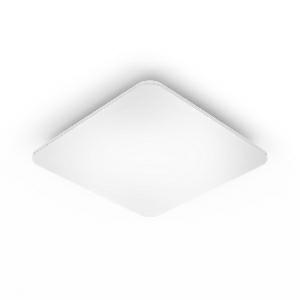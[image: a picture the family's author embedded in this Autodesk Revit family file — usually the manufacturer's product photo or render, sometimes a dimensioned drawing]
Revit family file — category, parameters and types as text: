
# Revit family: rs_pro_led_q1_007133
name_source: partatom
category: Leuchten
revit_build: Autodesk Revit 2016 (Build: 20190508_0715(x64)
units: mm (PartAtom-declared; Revit-internal decimal feet)

## family parameters
Basisbauteil = Fläche
Beim Laden mit Abzugskörper schneiden = Nein
Bemaßung runder Anschluss = Durchmesser verwenden
Gemeinsam genutzt = Nein
Lichtquelle = Nein
Raumberechnungspunkt = Nein
Teiletyp = Normal

## types (1)
- RS PRO LED Q1 (1 x , 2350 lm, 3000 K)
    Beschreibung = Dimensions (L x W x H): 56 x 331 x 331 mm; Mains power supply: 220 – 240 V / 50 – 60 Hz; Sensor Technology: High frequency; Transmitter power: < 1 mW; HF-system: 5,8 GHz; Output: 26 W; Interconnection: Yes; Type of interconnection: Master/master, Master/slave; Luminous flux: 2350 lm; Colour temperature: 3000 K; Colour variation LED: SDCM3; Colour Rendering Index CRI: 80-89; With lamp: Yes, STEINEL LED system; Lamp: LED cannot be replaced; LED life expectancy (max. °C): 50000 h; Drop in luminous flux in accordance with LM80: L70B10; Base: without; LED cooling system: Passive Thermo Control; With motion detector: Yes; Detection: also through glass, wood and stud walls; Detection angle: 360 °; Angle of aperture: 160 °; Capability of masking out individual segments: Yes; Electronic scalability: Yes; Mechanical scalability: No; Reach, radial: Ø 8 m (50 m²); Reach, tangential: Ø 8 m (50 m²); Main light adjustable: 50 - 100 %; Continuous light: selectable; Photo-cell controller: Yes; Twilight setting: 2 – 2000 lx; Time setting: 5 sec – 15 min; Basic light level function: Yes; Basic light level function time: 10/30 min, all night; Functions: Group parameterisation, Manual ON / ON-OFF, Master/slave override, Neighbouring-group function; Soft light start: Yes; Impact resistance: IK03; IP-rating: IP20; Protection class: II; Ambient temperature: -10 – 50 °C; Housing material: Aluminium; Cover material: Plastic, opal; Manufacturer's Warranty: 5 years; Settings via: DIP switches, Potentiometers, Remote control, Smart Remote; With remote control: No; Version: warm white white; PU1, EAN: 4007841007133
    CIE Flux Codes = 46 77 95 100 100
    Color Rendering = 80-89
    Color Temperature = 3000 K
    Frequency = 50 Hz, 60 Hz
    Height = 331 mm
    Hersteller = Steinel
    Lamp Light Flux = 2350 lm
    Lamp count = 1
    Lampe = 1 x
    Length = 56 mm  [stored 0.183727 ft]
    Luminous efficacy = 90 lm/W
    ModVariant = Nein
    Modell = 007133
    Mounting Type = Surface mounted
    Number of Poles = 1
    OnlyDefault = Ja
    Power Factor = 1
    Product Name = RS PRO LED Q1
    Product group = Sensor-switched indoor light
    ProductGroupID = 30
    Protection Class = Protection class II
    Protection Degree = IP 20
    RlxData = <blob elided: 27469 chars, md5=ace1f765>
    Scheinlast = 26 VA
    Socket = socket
    Standby Power = 0 W
    System Light Flux = 2350 lm
    System Power = 26 W
    Typenbild = produkt1_007133.jpg
    Typenkommentare = Product without accessories
    URL = http://relux.com
    VarID = ---
    Voltage = 0 V
    Vorgabe-Ansicht = 1800 mm
    Weight = 0.00 kg
    Width = 331 mm

note: [stored X ft] marks values corroborated as IEEE doubles in the binary element streams (Revit-internal decimal feet)

## geometry (parser evidence)
native form markers: Blend x4, Sweep x10
no freeform markers — native parametric forms only
